# Revit family: Switch-Lutron-Palladiom_QS_Keypad_Control-Group_6 new
name_source: partatom
category: Lighting Devices
revit_build: Autodesk Revit 2017 (Build: 20160225_1515(x64)
units: mm (PartAtom-declared; Revit-internal decimal feet)

## family parameters
Cut with Voids When Loaded = No
Host = Face
Maintain Annotation Orientation = Yes
OmniClass Number = 23.85.80.11.27
OmniClass Title = Lighting Controls
Part Type = Switch
Room Calculation Point = No
Round Connector Dimension = Use Radius
Shared = No

## types (1)
- Not a Type - Load Type Catalog
    (1) Quantum = No
    (1) US Faceplate Style = No
    (2) Square Faceplate Style = Yes
    (2) myRoom = No
    (3) HomeWorks QS = Yes
    Assembly Code = D5020120
    Button Array Gap Width = 0' - 0 9/16"
    Button Array Height = 0' - 2 13/16"
    Button Array Width = 0' - 1 7/32"
    Button Column 1 Button Selection = n_Button_Array IC : Standard
    Button Column 2 Button Selection = n_Button_Array IC : Standard
    Button Column 3 Button Selection = n_Button_Array IC : Standard
    Button Column 4 Button Selection = n_Button_Array IC : Standard
    Button Depth = 0' - 0 3/32"
    Button Gap Width = 0' - 0 1/32"
    Button Height for Quantity 2 = 0' - 1 3/8"
    Button Height for Quantity 3 = 0' - 0 29/32"
    Button Height for Quantity 4 = 0' - 0 11/16"
    Button Width = 0' - 1 1/4"
    Cost = 0 $
    Default Elevation = 3' - 6"
    Description = Keypad Control
    Device Depth from Wall = 0' - 0 11/32"
    Device Finish Material = Glass - Lutron - Black - Clear
    Device Recess Depth = 0' - 0 11/32"
    Faceplate Finish Material = Glass - Lutron - Black - Clear
    Faceplate Style Selection = 2
    Faceplate Visibility = Yes
    Finish Code = CBL
    Instruction Sheet Link = http://www.lutron.com
    Manufacturer = Lutron Electronics Co., Inc
    Manufacturer Fax Number = 610-282-1243
    Material Sequence Code = 3212
    Model = See Device Model Numbers Below
    Performance URL = http://www.lutron.com
    Plan Scale = 96
    Plate Depth = 0' - 0 3/16"
    Product Documentation Link = http://www.lutron.com
    Product Name = QS Wired Palladiom Keypad
    Product Page URL = http://www.lutron.com
    Series = Palladiom
    Square 1 Column Plate Width = 0' - 3 3/4"
    Square 2 Column Plate Width = 0' - 4 1/32"
    Square 3 Column Plate Width = 0' - 6 9/32"
    Square 4 Column Plate Width = 0' - 7 5/8"
    Square Plate Height = 0' - 3 3/4"
    System Type Selection = 3
    URL = http://www.lutron.com
    US 1 Gang Plate Width = 0' - 2 29/32"
    US 2 Gang Plate Width = 0' - 4 13/16"
    US 3 Gang Plate Width = 0' - 6 19/32"
    US 4 Gang Plate Width = 0' - 8 13/32"
    US Plate Height = 0' - 4 11/16"
    Version = 2017 - v2.0b
    Video Link = https://www.youtube.com
    Warranty URL = http://www.lutron.com
    White Backlighting = Yes

## geometry (parser evidence)
native form markers: Sweep x6
no freeform markers — native parametric forms only
